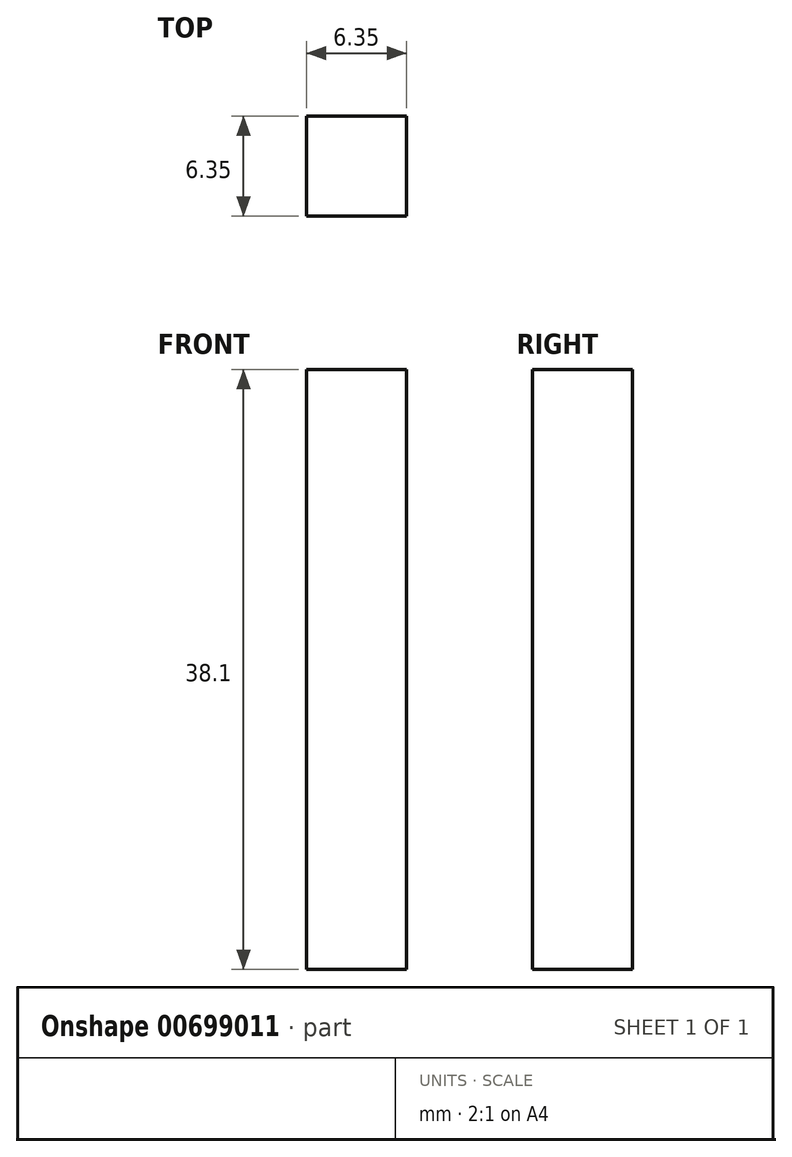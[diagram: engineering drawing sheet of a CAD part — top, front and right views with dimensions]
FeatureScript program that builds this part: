
annotation { "Feature Type Name" : "Feature", "Feature Type Description" : "" }
export const myFeature = defineFeature(function(context is Context, id is Id, definition is map)
    precondition{}
    {
        {
            var Q0;
            Q0=qCreatedBy(makeId("Front.planeOp"),FACE);
            var sketch = newSketch(context, id + "F0", { "sketchPlane" : qUnion([Q0])});
            skLineSegment(sketch, "E0", {"start": v(-47.26, 15.98) * mm, "end": v(-47.26, 54.08) * mm});
            skLineSegment(sketch, "E1", {"start": v(-47.26, 54.08) * mm, "end": v(-40.9, 54.08) * mm});
            skLineSegment(sketch, "E2", {"start": v(-40.9, 54.08) * mm, "end": v(-40.9, 15.98) * mm});
            skLineSegment(sketch, "E3", {"start": v(-40.9, 15.98) * mm, "end": v(-47.26, 15.98) * mm});
            skSolve(sketch);
        }
        {
            var Q0;
            Q0=makeQuery(id+"F0.imprint","IMPRINT",FACE,{"disambiguationData":[TD([[makeQuery(id+"F0.imprint","IMPRINT",EDGE,{"derivedFrom":sQuery(id+"F0.wireOp",EDGE,"E0")}),-1.0]])]});
            extrude(context, id + "F1", {"entities" : qUnion([Q0]), "depth" : 6.35 * mm, "offsetDistance" : 25.4 * mm});
        }
    });
